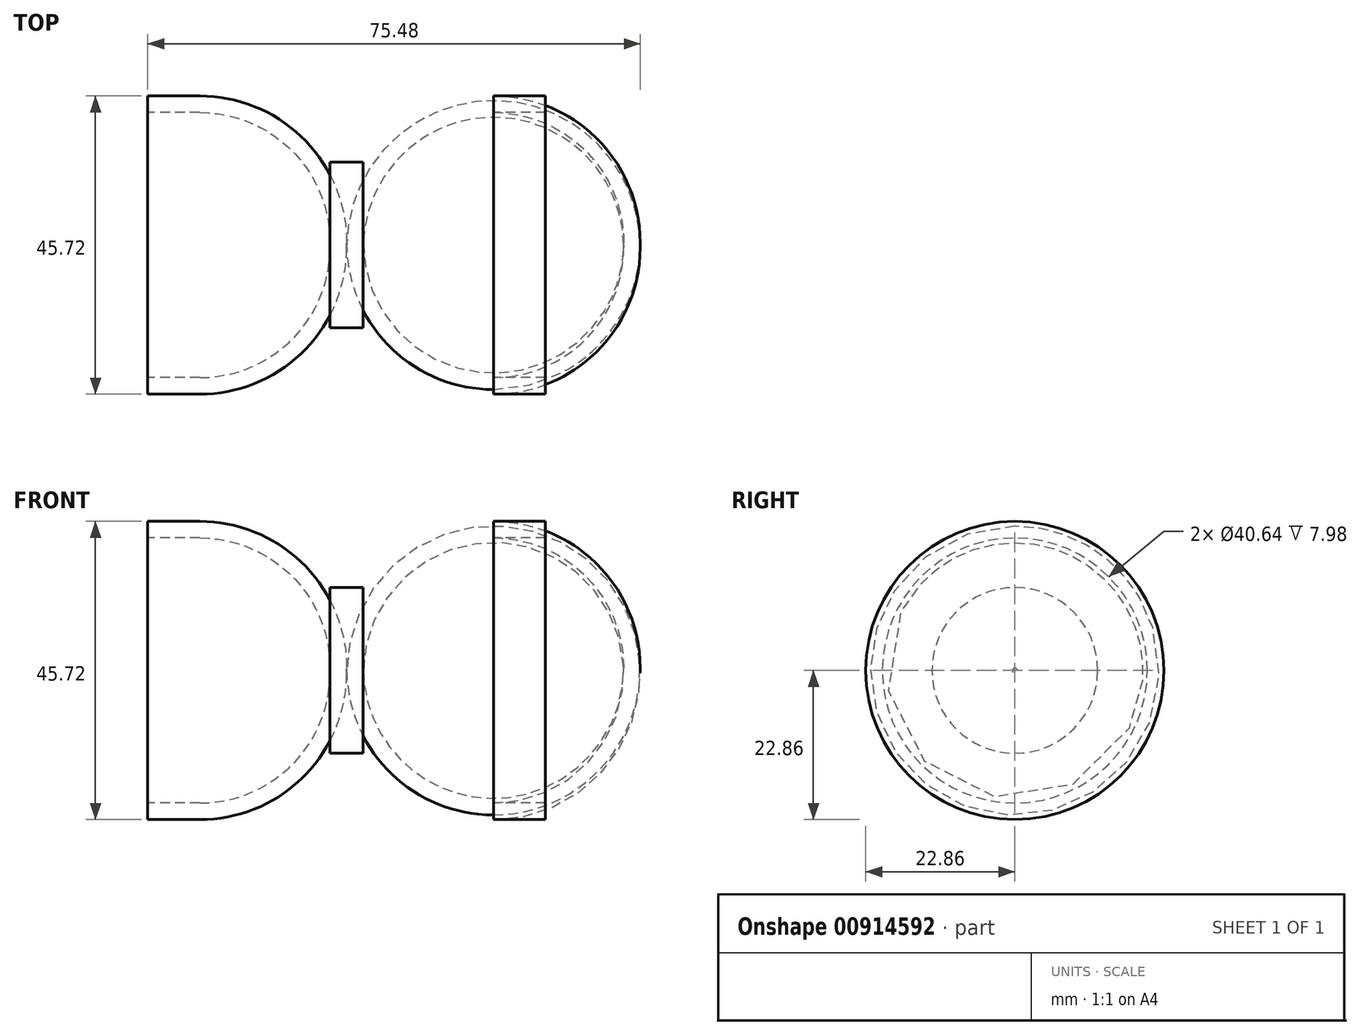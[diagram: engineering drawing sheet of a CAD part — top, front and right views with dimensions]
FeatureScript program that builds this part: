
annotation { "Feature Type Name" : "Feature", "Feature Type Description" : "" }
export const myFeature = defineFeature(function(context is Context, id is Id, definition is map)
    precondition{}
    {
        {
            var Q0;
            Q0=qCreatedBy(makeId("Right.planeOp"),FACE);
            var sketch = newSketch(context, id + "F0", { "sketchPlane" : qUnion([Q0])});
            skCircle(sketch, "E0", {"center": v(0, 0) * mm, "radius": 22.86 * mm});
            skSolve(sketch);
        }
        {
            var Q0;
            Q0=makeQuery(id+"F0.imprint","IMPRINT",FACE,{"disambiguationData":[TD([[makeQuery(id+"F0.imprint","IMPRINT",EDGE,{"derivedFrom":sQuery(id+"F0.wireOp",EDGE,"E0")}),1.0]])]});
            extrude(context, id + "F1", {"entities" : qUnion([Q0]), "depth" : 30.48 * mm, "offsetDistance" : 25.4 * mm});
        }
        {
            var Q0;
            Q0=makeQuery(id+"F1.opExtrude","CAP_FACE",FACE,{"disambiguationData":[OSD([sQuery(id+"F0.wireOp",EDGE,"E0")])],"isStart":false});
            shell(context, id + "F2", {"entities" : qUnion([Q0]), "thickness" : 2.54 * mm});
        }
        {
            var Q0;
            {var subQ0=sQuery(id+"F0.wireOp",EDGE,"E0");Q0=makeQuery(id+"F2.opShell","OFFSET_EDGE",EDGE,{"disambiguationData":[OSD([subQ0]),TDD([makeQuery(id+"F1.opExtrude","CAP_EDGE",EDGE,{"disambiguationData":[OSD([subQ0])],"isStart":true})])]});}
            fillet(context, id + "F3", {"entities" : qUnion([Q0]), "radius" : 19.96 * mm, "tangentPropagation" : true, "allowEdgeOverflow" : false});
        }
        {
            var Q0;
            Q0=makeQuery(id+"F1.opExtrude","CAP_EDGE",EDGE,{"disambiguationData":[OSD([sQuery(id+"F0.wireOp",EDGE,"E0")])],"isStart":true});
            fillet(context, id + "F4", {"entities" : qUnion([Q0]), "radius" : 22.5 * mm, "tangentPropagation" : true, "allowEdgeOverflow" : false});
        }
        {
            var Q0;
            Q0=qCreatedBy(makeId("Right.planeOp"),FACE);
            cPlane(context, id + "F5", {"entities" : qUnion([Q0]), "cplaneType" : CPlaneType.OFFSET, "offset" : 30.48 * mm, "oppositeDirection" : true, "width" : 152.4 * mm, "height" : 152.4 * mm});
        }
        {
            var Q0;
            Q0=qCreatedBy(id+"F5.planeOp",FACE);
            var sketch = newSketch(context, id + "F6", { "sketchPlane" : qUnion([Q0])});
            skCircle(sketch, "E1", {"center": v(0, 0) * mm, "radius": 22.86 * mm});
            skLineSegment(sketch, "E2", {"start": v(0, 0) * mm, "end": v(0, 22.86) * mm});
            skLineSegment(sketch, "E3", {"start": v(0, 0) * mm, "end": v(22.86, 0) * mm});
            skLineSegment(sketch, "E4", {"start": v(0, 0) * mm, "end": v(0, -22.86) * mm});
            skLineSegment(sketch, "E5", {"start": v(0, 0) * mm, "end": v(-22.86, 0) * mm});
            skPoint(sketch, "E6.end.orphan", {"position": v(16.16, 16.16) * mm});
            skLineSegment(sketch, "E7", {"start": v(0, 0) * mm, "end": v(16.16, -16.16) * mm});
            skLineSegment(sketch, "E8", {"start": v(0, 0) * mm, "end": v(16.16, 16.16) * mm});
            skLineSegment(sketch, "E9", {"start": v(0, 0) * mm, "end": v(-16.16, 16.16) * mm});
            skLineSegment(sketch, "E10", {"start": v(0, 0) * mm, "end": v(-16.16, -16.16) * mm});
            skLineSegment(sketch, "E11", {"start": v(0, 0) * mm, "end": v(21.12, -8.75) * mm});
            skLineSegment(sketch, "E12", {"start": v(0, 0) * mm, "end": v(8.75, 21.12) * mm});
            skLineSegment(sketch, "E13", {"start": v(0, 0) * mm, "end": v(-8.75, -21.12) * mm});
            skLineSegment(sketch, "E14", {"start": v(0, 0) * mm, "end": v(-21.12, 8.75) * mm});
            skLineSegment(sketch, "E15", {"start": v(0, 0) * mm, "end": v(8.75, -21.12) * mm});
            skLineSegment(sketch, "E16", {"start": v(0, 0) * mm, "end": v(-8.75, 21.12) * mm});
            skLineSegment(sketch, "E17", {"start": v(0, 0) * mm, "end": v(21.12, 8.75) * mm});
            skLineSegment(sketch, "E18", {"start": v(0, 0) * mm, "end": v(-21.12, -8.75) * mm});
            skSolve(sketch);
        }
        {
            var Q0;
            Q0=makeQuery(id+"F6.imprint","IMPRINT",FACE,{"disambiguationData":[TD([[makeQuery(id+"F6.imprint","IMPRINT",EDGE,{"derivedFrom":sQuery(id+"F6.wireOp",EDGE,"E1")}),1.0]])]});
            extrude(context, id + "F7", {"entities" : qUnion([Q0]), "depth" : 30.48 * mm, "offsetDistance" : 25.4 * mm});
        }
        {
            var Q0;
            Q0=makeQuery(id+"F7.opExtrude","CAP_FACE",FACE,{"disambiguationData":[OSD([sQuery(id+"F6.wireOp",EDGE,"E1")])],"isStart":true});
            shell(context, id + "F8", {"entities" : qUnion([Q0]), "thickness" : 2.54 * mm});
        }
        {
            var Q0;
            {var subQ0=sQuery(id+"F6.wireOp",EDGE,"E1");Q0=makeQuery(id+"F8.opShell","OFFSET_EDGE",EDGE,{"disambiguationData":[OSD([subQ0]),TDD([makeQuery(id+"F7.opExtrude","CAP_EDGE",EDGE,{"disambiguationData":[OSD([subQ0])],"isStart":false})])]});}
            fillet(context, id + "F9", {"entities" : qUnion([Q0]), "radius" : 19.96 * mm, "tangentPropagation" : true, "allowEdgeOverflow" : false});
        }
        {
            var Q0;
            Q0=makeQuery(id+"F7.opExtrude","CAP_EDGE",EDGE,{"disambiguationData":[OSD([sQuery(id+"F6.wireOp",EDGE,"E1")])],"isStart":false});
            fillet(context, id + "F10", {"entities" : qUnion([Q0]), "radius" : 22.5 * mm, "tangentPropagation" : true, "allowEdgeOverflow" : false});
        }
        {
            var Q0;
            Q0=qCreatedBy(makeId("Right.planeOp"),FACE);
            var sketch = newSketch(context, id + "F11", { "sketchPlane" : qUnion([Q0])});
            skCircle(sketch, "E19", {"center": v(0, 0) * mm, "radius": 12.7 * mm});
            skSolve(sketch);
        }
        {
            var Q0;
            Q0 = qSketchRegion(id + "F11", true);
            extrude(context, id + "F12", {"entities" : qUnion([Q0]), "endBound" : BoundingType.SYMMETRIC, "depth" : 5.08 * mm, "offsetDistance" : 25.4 * mm, "hasSecondDirection" : true, "secondDirectionOppositeDirection" : true, "secondDirectionDepth" : 25.4 * mm});
        }
    });
